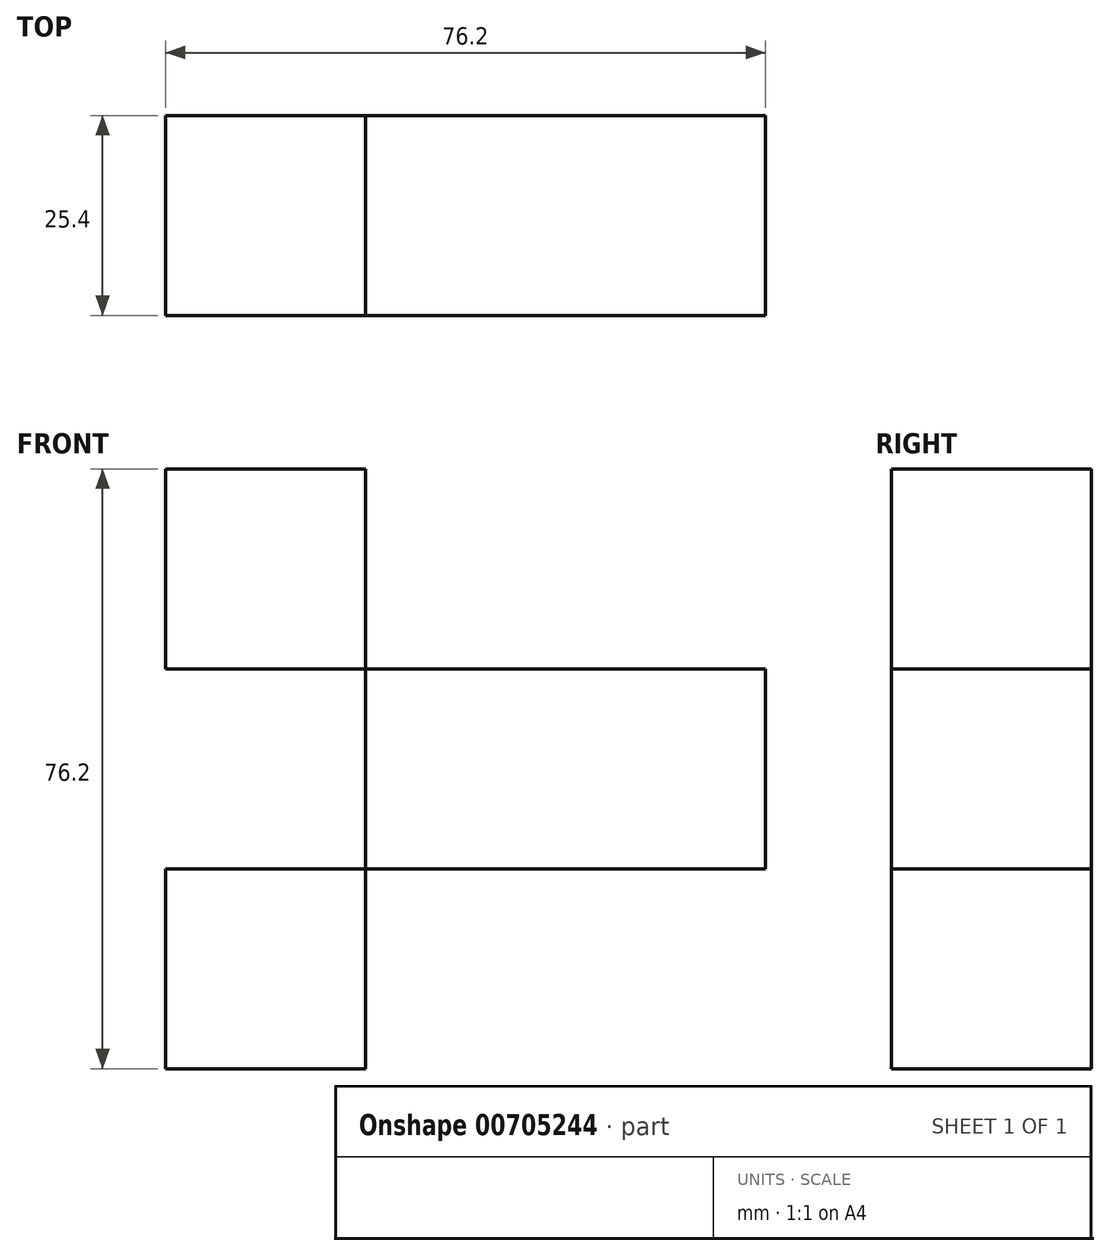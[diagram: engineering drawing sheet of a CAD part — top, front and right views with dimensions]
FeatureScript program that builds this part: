
annotation { "Feature Type Name" : "Feature", "Feature Type Description" : "" }
export const myFeature = defineFeature(function(context is Context, id is Id, definition is map)
    precondition{}
    {
        {
            var Q0;
            Q0=qCreatedBy(makeId("Front.planeOp"),FACE);
            var sketch = newSketch(context, id + "F0", { "sketchPlane" : qUnion([Q0])});
            skLineSegment(sketch, "E0.bottom", {"start": v(0, 50.8) * mm, "end": v(-25.4, 50.8) * mm});
            skLineSegment(sketch, "E0.top", {"start": v(0, 25.4) * mm, "end": v(-25.4, 25.4) * mm});
            skLineSegment(sketch, "E0.left", {"start": v(0, 50.8) * mm, "end": v(0, 25.4) * mm});
            skLineSegment(sketch, "E0.right", {"start": v(-25.4, 50.8) * mm, "end": v(-25.4, 25.4) * mm});
            skLineSegment(sketch, "E1.bottom", {"start": v(-25.4, 25.4) * mm, "end": v(0, 25.4) * mm});
            skLineSegment(sketch, "E1.top", {"start": v(-25.4, 0) * mm, "end": v(0, 0) * mm});
            skLineSegment(sketch, "E1.left", {"start": v(-25.4, 25.4) * mm, "end": v(-25.4, 0) * mm});
            skLineSegment(sketch, "E1.right", {"start": v(0, 25.4) * mm, "end": v(0, 0) * mm});
            skLineSegment(sketch, "E2.top", {"start": v(-25.4, -25.4) * mm, "end": v(0, -25.4) * mm});
            skLineSegment(sketch, "E2.left", {"start": v(-25.4, 0) * mm, "end": v(-25.4, -25.4) * mm});
            skLineSegment(sketch, "E2.right", {"start": v(0, 0) * mm, "end": v(0, -25.4) * mm});
            skLineSegment(sketch, "E3.bottom", {"start": v(0, 25.4) * mm, "end": v(25.4, 25.4) * mm});
            skLineSegment(sketch, "E3.top", {"start": v(0, 0) * mm, "end": v(25.4, 0) * mm});
            skLineSegment(sketch, "E3.right", {"start": v(25.4, 25.4) * mm, "end": v(25.4, 0) * mm});
            skLineSegment(sketch, "E4.bottom", {"start": v(25.4, 25.4) * mm, "end": v(50.8, 25.4) * mm});
            skLineSegment(sketch, "E4.top", {"start": v(25.4, 0) * mm, "end": v(50.8, 0) * mm});
            skLineSegment(sketch, "E4.right", {"start": v(50.8, 25.4) * mm, "end": v(50.8, 0) * mm});
            skLineSegment(sketch, "E5.bottom", {"start": v(50.8, 0) * mm, "end": v(25.4, 0) * mm});
            skLineSegment(sketch, "E5.top", {"start": v(50.8, -25.4) * mm, "end": v(25.4, -25.4) * mm});
            skLineSegment(sketch, "E5.left", {"start": v(50.8, 0) * mm, "end": v(50.8, -25.4) * mm});
            skLineSegment(sketch, "E5.right", {"start": v(25.4, 0) * mm, "end": v(25.4, -25.4) * mm});
            skSolve(sketch);
        }
        {
            var Q0;
            Q0=makeQuery(id+"F0.imprint","IMPRINT",FACE,{"disambiguationData":[TD([[makeQuery(id+"F0.imprint","IMPRINT",EDGE,{"derivedFrom":sQuery(id+"F0.wireOp",EDGE,"E0.bottom")}),1.0]])]});
            var Q1;
            Q1=makeQuery(id+"F0.imprint","IMPRINT",FACE,{"disambiguationData":[TD([[makeQuery(id+"F0.imprint","IMPRINT",EDGE,{"derivedFrom":sQuery(id+"F0.wireOp",EDGE,"E1.bottom")}),-1.0]])]});
            var Q2;
            Q2=makeQuery(id+"F0.imprint","IMPRINT",FACE,{"disambiguationData":[TD([[makeQuery(id+"F0.imprint","IMPRINT",EDGE,{"derivedFrom":sQuery(id+"F0.wireOp",EDGE,"E4.bottom")}),-1.0]])]});
            var Q3;
            Q3=makeQuery(id+"F0.imprint","IMPRINT",FACE,{"disambiguationData":[TD([[makeQuery(id+"F0.imprint","IMPRINT",EDGE,{"derivedFrom":sQuery(id+"F0.wireOp",EDGE,"E3.bottom")}),-1.0]])]});
            var Q4;
            Q4=makeQuery(id+"F0.imprint","IMPRINT",FACE,{"disambiguationData":[TD([[makeQuery(id+"F0.imprint","IMPRINT",EDGE,{"derivedFrom":sQuery(id+"F0.wireOp",EDGE,"E1.top")}),-1.0]])]});
            var Q5;
            Q5=makeQuery(id+"F0.imprint","IMPRINT",FACE,{"disambiguationData":[TD([[makeQuery(id+"F0.imprint","IMPRINT",EDGE,{"derivedFrom":sQuery(id+"F0.wireOp",EDGE,"E5.bottom")}),1.0]])]});
            extrude(context, id + "F1", {"entities" : qUnion([Q0, Q1, Q2, Q3, Q4, Q5]), "depth" : 25.4 * mm, "offsetDistance" : 25.4 * mm});
        }
    });
